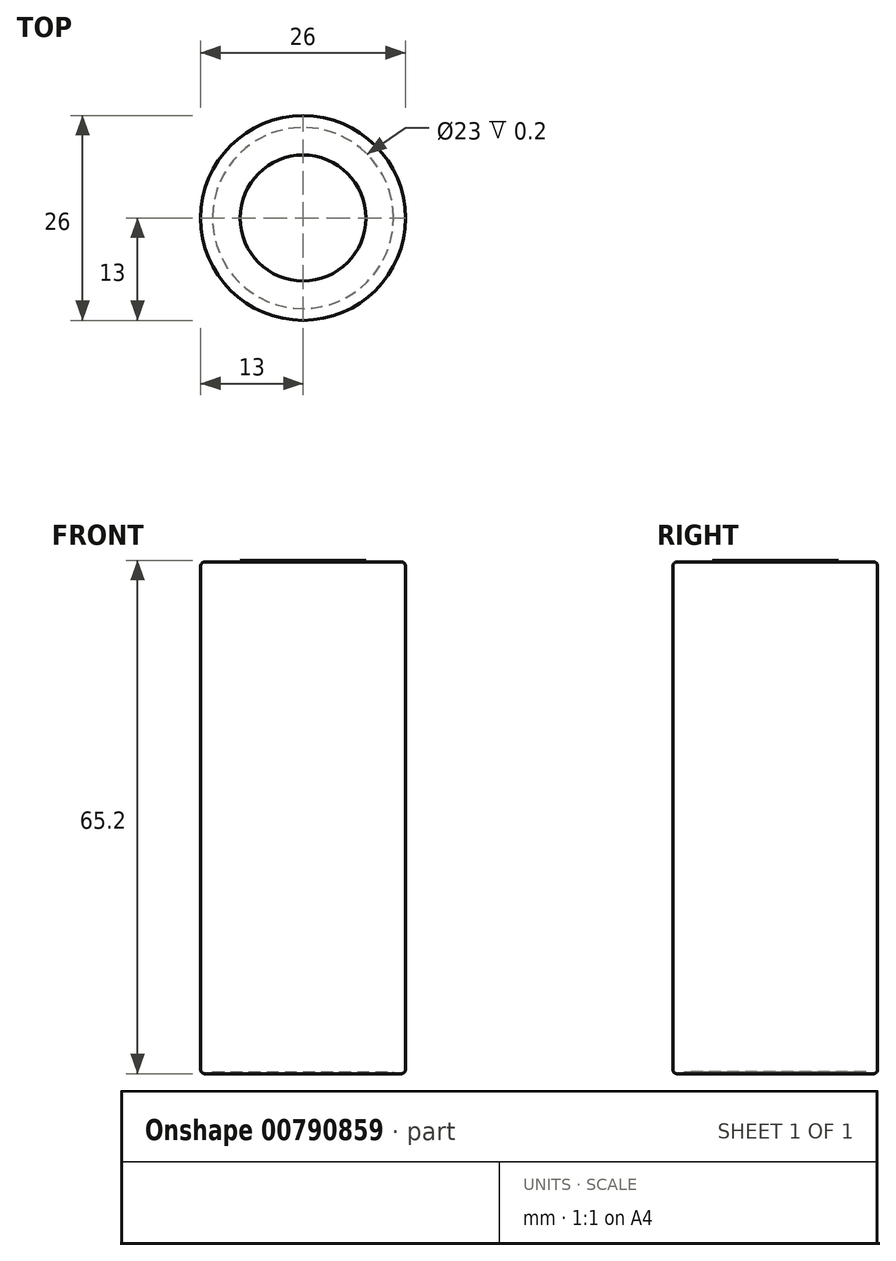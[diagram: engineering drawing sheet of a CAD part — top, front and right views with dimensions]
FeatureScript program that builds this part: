
annotation { "Feature Type Name" : "Feature", "Feature Type Description" : "" }
export const myFeature = defineFeature(function(context is Context, id is Id, definition is map)
    precondition{}
    {
        {
            var Q0;
            Q0=qCreatedBy(makeId("Top.planeOp"),FACE);
            var sketch = newSketch(context, id + "F0", { "sketchPlane" : qUnion([Q0])});
            skCircle(sketch, "E0", {"center": v(0, 0) * mm, "radius": 13 * mm});
            skSolve(sketch);
        }
        {
            var Q0;
            Q0=qSketchRegion(id+"F0",true);
            extrude(context, id + "F1", {"entities" : qUnion([Q0]), "depth" : 65 * mm, "offsetDistance" : 25 * mm});
        }
        {
            var Q0;
            Q0=makeQuery(id+"F1.opExtrude","CAP_FACE",FACE,{"disambiguationData":[OSD([sQuery(id+"F0.wireOp",EDGE,"E0")])],"isStart":false});
            var sketch = newSketch(context, id + "F2", { "sketchPlane" : qUnion([Q0])});
            skCircle(sketch, "E1", {"center": v(0, 0) * mm, "radius": 8 * mm});
            skSolve(sketch);
        }
        {
            var Q0;
            Q0=qSketchRegion(id+"F2",true);
            extrude(context, id + "F3", {"entities" : qUnion([Q0]), "depth" : 0.2 * mm, "offsetDistance" : 25 * mm});
        }
        {
            var Q0;
            Q0=makeQuery(id+"F1.opExtrude","CAP_FACE",FACE,{"disambiguationData":[OSD([sQuery(id+"F0.wireOp",EDGE,"E0")])],"isStart":true});
            var sketch = newSketch(context, id + "F4", { "sketchPlane" : qUnion([Q0])});
            skCircle(sketch, "E2", {"center": v(0, 0) * mm, "radius": 11.5 * mm});
            skSolve(sketch);
        }
        {
            var Q0;
            Q0=qSketchRegion(id+"F4",true);
            extrude(context, id + "F5", {"entities" : qUnion([Q0]), "operationType" : NewBodyOperationType.REMOVE, "oppositeDirection" : true, "depth" : 0.2 * mm, "offsetDistance" : 25 * mm});
        }
        {
            var Q0;
            Q0=makeQuery(id+"F5.boolean.opBoolean","COPY",FACE,{"derivedFrom":makeQuery(id+"F5.opExtrude","CAP_FACE",FACE,{"disambiguationData":[OSD([sQuery(id+"F4.wireOp",EDGE,"E2")])],"isStart":false})});
            var sketch = newSketch(context, id + "F6", { "sketchPlane" : qUnion([Q0])});
            skCircle(sketch, "E3", {"center": v(0, 0) * mm, "radius": 11.5 * mm});
            skSolve(sketch);
        }
        {
            var Q0;
            Q0=qSketchRegion(id+"F6",true);
            extrude(context, id + "F7", {"entities" : qUnion([Q0]), "depth" : 0.2 * mm, "offsetDistance" : 25 * mm});
        }
        {
            var Q0;
            Q0=makeQuery(id+"F1.opExtrude","CAP_EDGE",EDGE,{"disambiguationData":[OSD([sQuery(id+"F0.wireOp",EDGE,"E0")])],"isStart":false});
            var Q1;
            Q1=makeQuery(id+"F1.opExtrude","CAP_EDGE",EDGE,{"disambiguationData":[OSD([sQuery(id+"F0.wireOp",EDGE,"E0")])],"isStart":true});
            fillet(context, id + "F8", {"entities" : qUnion([Q0, Q1]), "radius" : 0.5 * mm, "tangentPropagation" : true, "allowEdgeOverflow" : false});
        }
    });
